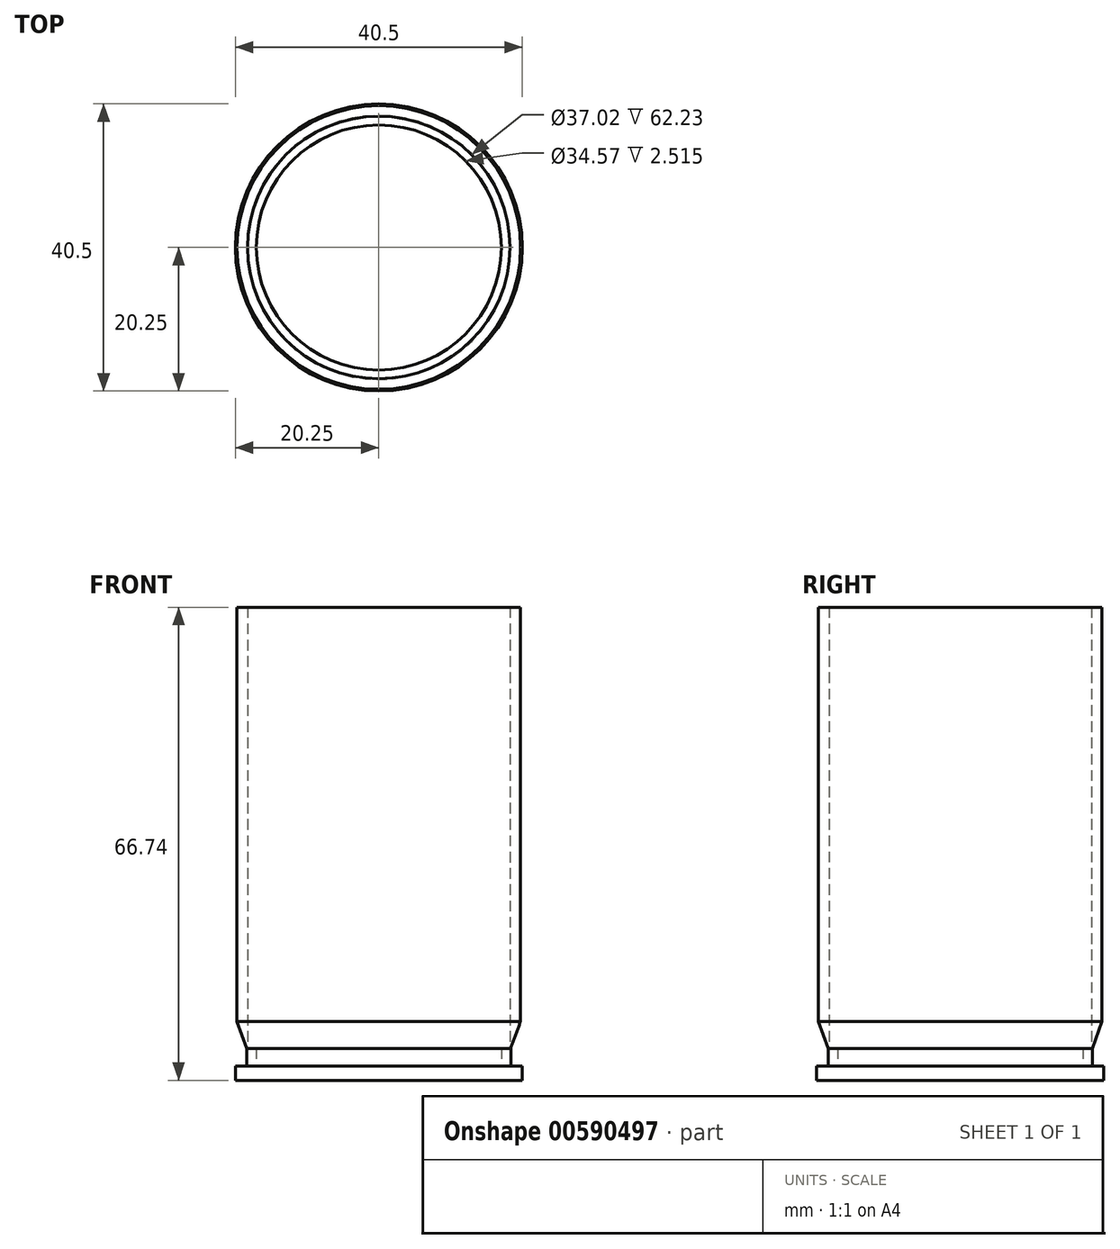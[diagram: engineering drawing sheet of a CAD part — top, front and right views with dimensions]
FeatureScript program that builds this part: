
annotation { "Feature Type Name" : "Feature", "Feature Type Description" : "" }
export const myFeature = defineFeature(function(context is Context, id is Id, definition is map)
    precondition{}
    {
        {
            var Q0;
            Q0=qCreatedBy(makeId("Top.planeOp"),FACE);
            var sketch = newSketch(context, id + "F0", { "sketchPlane" : qUnion([Q0])});
            skCircle(sketch, "E0", {"center": v(0, 0) * mm, "radius": 20 * mm});
            skCircle(sketch, "E1", {"center": v(0, 0) * mm, "radius": 18.5 * mm});
            skSolve(sketch);
        }
        {
            var Q0;
            Q0 = qSketchRegion(id + "F0", true);
            extrude(context, id + "F1", {"entities" : qUnion([Q0]), "depth" : 63.5 * mm, "offsetDistance" : 25.4 * mm});
        }
        {
            var Q0;
            Q0=makeQuery(id+"F1.opExtrude","CAP_EDGE",EDGE,{"disambiguationData":[OSD([sQuery(id+"F0.wireOp",EDGE,"E0")])],"isStart":true});
            chamfer(context, id + "F2", {"entities" : qUnion([Q0]), "chamferType" : ChamferType.OFFSET_ANGLE, "width" : 5.08 * mm, "oppositeDirection" : false, "angle" : 20 * degree, "tangentPropagation" : true});
        }
        {
            var Q0;
            Q0=qCreatedBy(makeId("Top.planeOp"),FACE);
            var sketch = newSketch(context, id + "F3", { "sketchPlane" : qUnion([Q0])});
            skCircle(sketch, "E2", {"center": v(0, 0) * mm, "radius": 18.62 * mm});
            skCircle(sketch, "E3", {"center": v(0, 0) * mm, "radius": 17.28 * mm});
            skSolve(sketch);
        }
        {
            var Q0;
            Q0 = qSketchRegion(id + "F3", true);
            extrude(context, id + "F4", {"entities" : qUnion([Q0]), "operationType" : NewBodyOperationType.ADD, "depth" : 2.54 * mm, "offsetDistance" : 25.4 * mm, "symmetric" : true});
        }
        {
            var Q0;
            Q0=qCreatedBy(makeId("Top.planeOp"),FACE);
            cPlane(context, id + "F5", {"entities" : qUnion([Q0]), "cplaneType" : CPlaneType.OFFSET, "offset" : 1.24 * mm, "oppositeDirection" : true, "width" : 152.4 * mm, "height" : 152.4 * mm});
        }
        {
            var Q0;
            Q0=qCreatedBy(id+"F5.planeOp",FACE);
            var sketch = newSketch(context, id + "F6", { "sketchPlane" : qUnion([Q0])});
            skCircle(sketch, "E4", {"center": v(0, 0) * mm, "radius": 20.25 * mm});
            skSolve(sketch);
        }
        {
            var Q0;
            Q0 = qSketchRegion(id + "F6", true);
            extrude(context, id + "F7", {"entities" : qUnion([Q0]), "operationType" : NewBodyOperationType.ADD, "oppositeDirection" : true, "depth" : 2 * mm, "offsetDistance" : 25.4 * mm});
        }
    });
